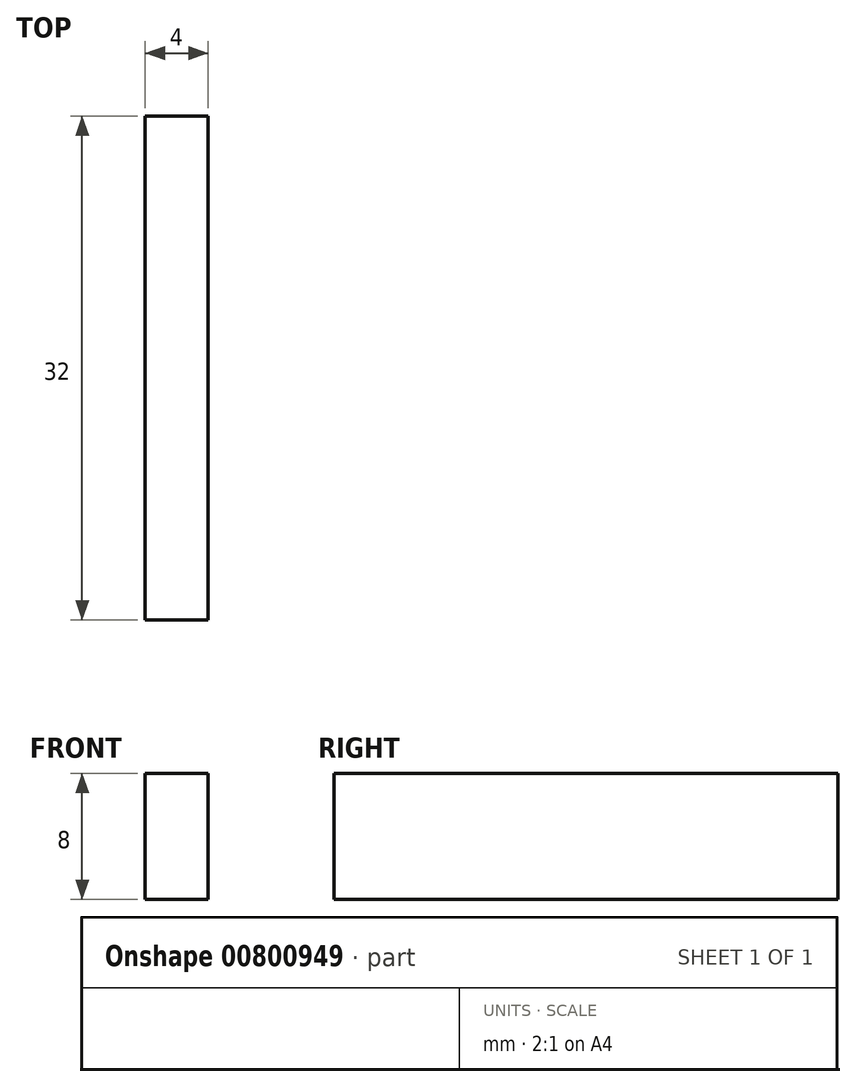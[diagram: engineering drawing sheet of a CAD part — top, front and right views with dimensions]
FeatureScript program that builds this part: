
annotation { "Feature Type Name" : "Feature", "Feature Type Description" : "" }
export const myFeature = defineFeature(function(context is Context, id is Id, definition is map)
    precondition{}
    {
        {
            var Q0;
            Q0=qCreatedBy(makeId("Top.planeOp"),FACE);
            var sketch = newSketch(context, id + "F0", { "sketchPlane" : qUnion([Q0])});
            skLineSegment(sketch, "E0.bottom", {"start": v(0, 0) * mm, "end": v(4, 0) * mm});
            skLineSegment(sketch, "E0.top", {"start": v(0, -32) * mm, "end": v(4, -32) * mm});
            skLineSegment(sketch, "E0.left", {"start": v(0, 0) * mm, "end": v(0, -32) * mm});
            skLineSegment(sketch, "E0.right", {"start": v(4, 0) * mm, "end": v(4, -32) * mm});
            skSolve(sketch);
        }
        {
            var Q0;
            Q0=makeQuery(id+"F0.imprint","IMPRINT",FACE,{"disambiguationData":[TD([[makeQuery(id+"F0.imprint","IMPRINT",EDGE,{"derivedFrom":sQuery(id+"F0.wireOp",EDGE,"E0.bottom")}),-1.0]])]});
            extrude(context, id + "F1", {"entities" : qUnion([Q0]), "depth" : 8 * mm, "offsetDistance" : 25 * mm});
        }
    });
